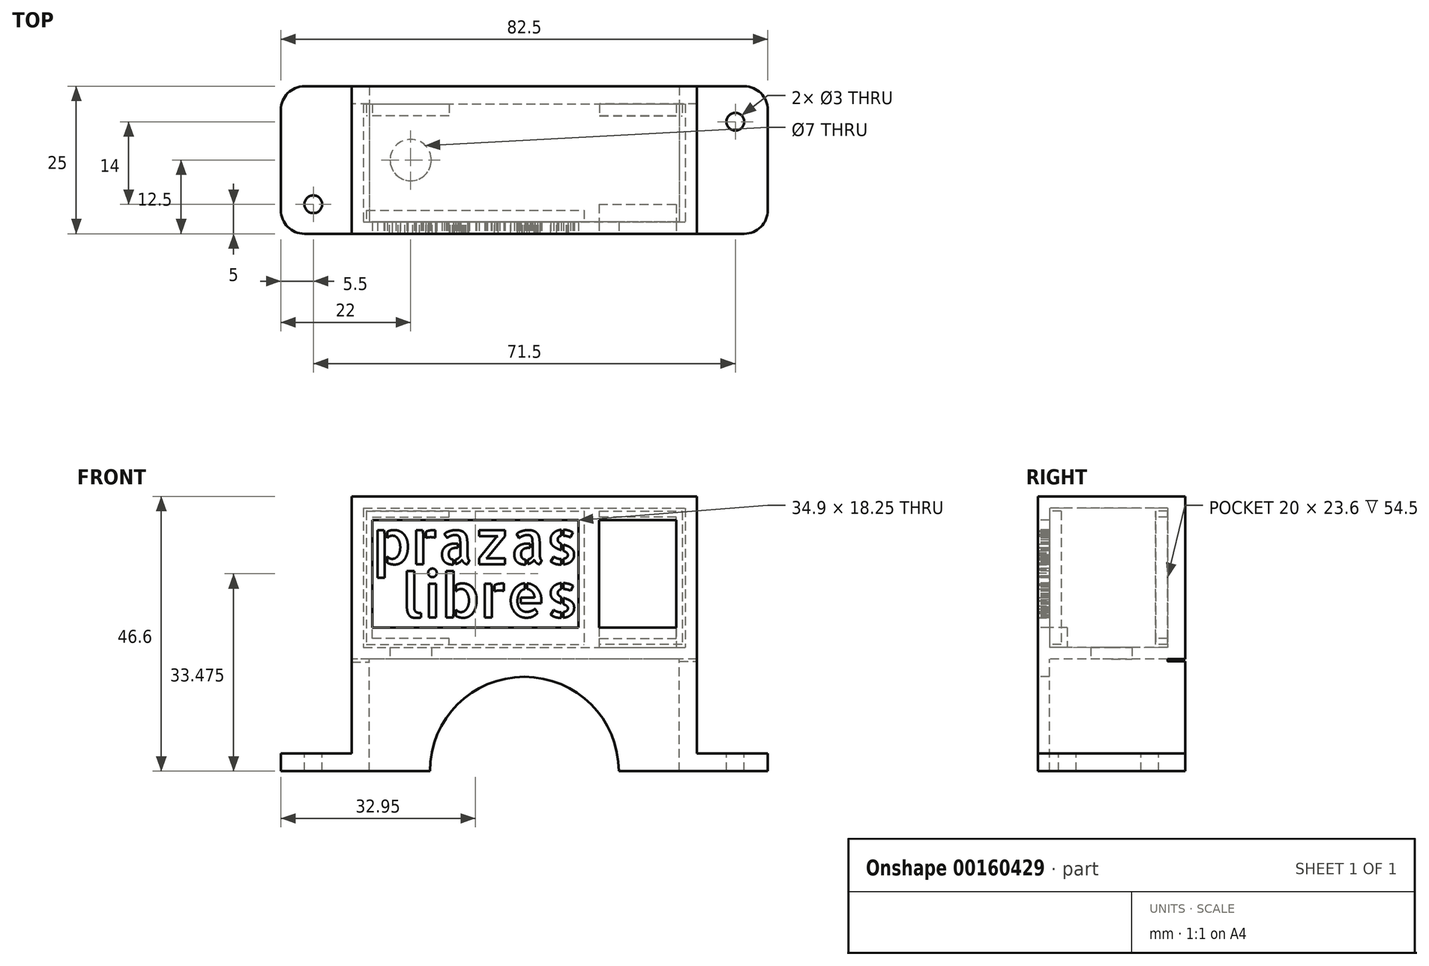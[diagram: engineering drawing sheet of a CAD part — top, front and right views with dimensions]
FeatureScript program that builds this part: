
annotation { "Feature Type Name" : "Feature", "Feature Type Description" : "" }
export const myFeature = defineFeature(function(context is Context, id is Id, definition is map)
    precondition{}
    {
        {
            var Q0;
            Q0=qCreatedBy(makeId("Front.planeOp"),FACE);
            var sketch = newSketch(context, id + "F0", { "sketchPlane" : qUnion([Q0])});
            skLineSegment(sketch, "E0.bottom", {"start": v(0, 0) * mm, "end": v(-58.5, 0) * mm});
            skLineSegment(sketch, "E0.top", {"start": v(0, 27.6) * mm, "end": v(-58.5, 27.6) * mm});
            skLineSegment(sketch, "E0.left", {"start": v(0, 0) * mm, "end": v(0, 27.6) * mm});
            skLineSegment(sketch, "E0.right", {"start": v(-58.5, 0) * mm, "end": v(-58.5, 27.6) * mm});
            skLineSegment(sketch, "E1.bottom", {"start": v(-3.5, 5.35) * mm, "end": v(-16.6, 5.35) * mm});
            skLineSegment(sketch, "E1.top", {"start": v(-3.5, 23.6) * mm, "end": v(-16.6, 23.6) * mm});
            skLineSegment(sketch, "E1.left", {"start": v(-3.5, 5.35) * mm, "end": v(-3.5, 23.6) * mm});
            skLineSegment(sketch, "E1.right", {"start": v(-16.6, 5.35) * mm, "end": v(-16.6, 23.6) * mm});
            skLineSegment(sketch, "E2", {"start": v(0, 0) * mm, "end": v(0, -16) * mm});
            skLineSegment(sketch, "E3", {"start": v(0, -16) * mm, "end": v(12, -16) * mm});
            skLineSegment(sketch, "E4", {"start": v(12, -16) * mm, "end": v(12, -19) * mm});
            skLineSegment(sketch, "E5", {"start": v(12, -19) * mm, "end": v(-3, -19) * mm});
            skLineSegment(sketch, "E6", {"start": v(-3, -19) * mm, "end": v(-3, 0) * mm});
            skLineSegment(sketch, "E7", {"start": v(-29.25, 49.54) * mm, "end": v(-29.25, -33.62) * mm, "construction": true});
            skLineSegment(sketch, "E8.MirrorCS", {"start": v(-58.5, 0) * mm, "end": v(-58.5, -16) * mm});
            skLineSegment(sketch, "E9.MirrorCS", {"start": v(-58.5, -16) * mm, "end": v(-70.5, -16) * mm});
            skLineSegment(sketch, "E10.MirrorCS", {"start": v(-70.5, -16) * mm, "end": v(-70.5, -19) * mm});
            skLineSegment(sketch, "E11.MirrorCS", {"start": v(-70.5, -19) * mm, "end": v(-55.5, -19) * mm});
            skLineSegment(sketch, "E12.MirrorCS", {"start": v(-55.5, -19) * mm, "end": v(-55.5, 0) * mm});
            skLineSegment(sketch, "E13.top", {"start": v(-56.5, 2) * mm, "end": v(-2, 2) * mm});
            skLineSegment(sketch, "E13.left", {"start": v(-56.5, 25.6) * mm, "end": v(-56.5, 2) * mm});
            skLineSegment(sketch, "E13.right", {"start": v(-2, 25.6) * mm, "end": v(-2, 2) * mm});
            skLineSegment(sketch, "E14", {"start": v(-55.5, -19) * mm, "end": v(-3, -19) * mm});
            skArc(sketch, "E15", {"start": v(-13.25, -19) * mm, "mid": v(-29.25, -3) * mm, "end": v(-45.25, -19) * mm});
            skLineSegment(sketch, "E16", {"start": v(-56.5, 25.6) * mm, "end": v(-2, 25.6) * mm});
            skLineSegment(sketch, "E17.bottom", {"start": v(-20.1, 23.6) * mm, "end": v(-55, 23.6) * mm});
            skLineSegment(sketch, "E17.top", {"start": v(-20.1, 5.35) * mm, "end": v(-55, 5.35) * mm});
            skLineSegment(sketch, "E17.left", {"start": v(-20.1, 23.6) * mm, "end": v(-20.1, 5.35) * mm});
            skLineSegment(sketch, "E17.right", {"start": v(-55, 23.6) * mm, "end": v(-55, 5.35) * mm});
            skLineSegment(sketch, "E18", {"start": v(-16.6, 5.35) * mm, "end": v(-16.6, 2) * mm});
            skLineSegment(sketch, "E19", {"start": v(-3.5, 5.35) * mm, "end": v(-3.5, 2) * mm});
            skLineSegment(sketch, "E20.bottom", {"start": v(-56, 25.1) * mm, "end": v(-19.1, 25.1) * mm});
            skLineSegment(sketch, "E20.top", {"start": v(-56, 2.5) * mm, "end": v(-19.1, 2.5) * mm});
            skLineSegment(sketch, "E20.left", {"start": v(-56, 25.1) * mm, "end": v(-56, 2.5) * mm});
            skLineSegment(sketch, "E20.right", {"start": v(-19.1, 25.1) * mm, "end": v(-19.1, 2.5) * mm});
            skText(sketch, "E21", { "text": "prazas", "fontName": "AllertaStencil-Regular.ttf"});
            skText(sketch, "E22", { "text": "libres", "fontName": "AllertaStencil-Regular.ttf"});
            skLineSegment(sketch, "E23", {"start": v(-3, -0.4) * mm, "end": v(0, -0.4) * mm});
            skLineSegment(sketch, "E24", {"start": v(-58.5, -0.5) * mm, "end": v(-55.5, -0.5) * mm});
            const initialGuessF0  = {"E21": [-0.055, 0.01608, 1, 0, 0.00752], "E22": [-0.05, 0.00705, 1, 0, 0.0075]};
            skSetInitialGuess(sketch, initialGuessF0);
            skSolve(sketch);
        }
        {
            var Q0;
            Q0=makeQuery(id+"F0.imprint","IMPRINT",FACE,{"disambiguationData":[TD([[makeQuery(id+"F0.imprint","IMPRINT",EDGE,{"derivedFrom":sQuery(id+"F0.wireOp",EDGE,"E0.top")}),1.0]])]});
            extrude(context, id + "F1", {"entities" : qUnion([Q0]), "oppositeDirection" : true, "depth" : 22 * mm});
        }
        {
            var Q0;
            Q0=makeQuery(id+"F0.imprint","IMPRINT",FACE,{"disambiguationData":[TD([[makeQuery(id+"F0.imprint","IMPRINT",EDGE,{"derivedFrom":sQuery(id+"F0.wireOp",EDGE,"1b1c06d7-5df4-4c5e-b730-0ffd46047cfb.sketch_text.stroke-0")}),-1.0]])]});
            var Q1;
            Q1=makeQuery(id+"F0.imprint","IMPRINT",FACE,{"disambiguationData":[TD([[makeQuery(id+"F0.imprint","IMPRINT",EDGE,{"derivedFrom":sQuery(id+"F0.wireOp",EDGE,"1b1c06d7-5df4-4c5e-b730-0ffd46047cfb.sketch_text.stroke-25")}),-1.0]])]});
            var Q2;
            Q2=makeQuery(id+"F0.imprint","IMPRINT",FACE,{"disambiguationData":[TD([[makeQuery(id+"F0.imprint","IMPRINT",EDGE,{"derivedFrom":sQuery(id+"F0.wireOp",EDGE,"1b1c06d7-5df4-4c5e-b730-0ffd46047cfb.sketch_text.stroke-16")}),1.0]])]});
            var Q3;
            Q3=makeQuery(id+"F0.imprint","IMPRINT",FACE,{"disambiguationData":[TD([[makeQuery(id+"F0.imprint","IMPRINT",EDGE,{"derivedFrom":sQuery(id+"F0.wireOp",EDGE,"1b1c06d7-5df4-4c5e-b730-0ffd46047cfb.sketch_text.stroke-38")}),-1.0]])]});
            var Q4;
            Q4=makeQuery(id+"F0.imprint","IMPRINT",FACE,{"disambiguationData":[TD([[makeQuery(id+"F0.imprint","IMPRINT",EDGE,{"derivedFrom":sQuery(id+"F0.wireOp",EDGE,"1b1c06d7-5df4-4c5e-b730-0ffd46047cfb.sketch_text.stroke-57")}),1.0]])]});
            var Q5;
            Q5=makeQuery(id+"F0.imprint","IMPRINT",FACE,{"disambiguationData":[TD([[makeQuery(id+"F0.imprint","IMPRINT",EDGE,{"derivedFrom":sQuery(id+"F0.wireOp",EDGE,"1b1c06d7-5df4-4c5e-b730-0ffd46047cfb.sketch_text.stroke-65")}),-1.0]])]});
            var Q6;
            Q6=makeQuery(id+"F0.imprint","IMPRINT",FACE,{"disambiguationData":[TD([[makeQuery(id+"F0.imprint","IMPRINT",EDGE,{"derivedFrom":sQuery(id+"F0.wireOp",EDGE,"1b1c06d7-5df4-4c5e-b730-0ffd46047cfb.sketch_text.stroke-75")}),-1.0]])]});
            var Q7;
            Q7=makeQuery(id+"F0.imprint","IMPRINT",FACE,{"disambiguationData":[TD([[makeQuery(id+"F0.imprint","IMPRINT",EDGE,{"derivedFrom":sQuery(id+"F0.wireOp",EDGE,"1b1c06d7-5df4-4c5e-b730-0ffd46047cfb.sketch_text.stroke-94")}),1.0]])]});
            var Q8;
            Q8=makeQuery(id+"F0.imprint","IMPRINT",FACE,{"disambiguationData":[TD([[makeQuery(id+"F0.imprint","IMPRINT",EDGE,{"derivedFrom":sQuery(id+"F0.wireOp",EDGE,"1b1c06d7-5df4-4c5e-b730-0ffd46047cfb.sketch_text.stroke-102")}),-1.0]])]});
            var Q9;
            Q9=makeQuery(id+"F0.imprint","IMPRINT",FACE,{"disambiguationData":[TD([[makeQuery(id+"F0.imprint","IMPRINT",EDGE,{"derivedFrom":sQuery(id+"F0.wireOp",EDGE,"71fc07e8-a1ba-411f-bdb7-0ce3e880cc4c.sketch_text.stroke-0")}),-1.0]])]});
            var Q10;
            Q10=makeQuery(id+"F0.imprint","IMPRINT",FACE,{"disambiguationData":[TD([[makeQuery(id+"F0.imprint","IMPRINT",EDGE,{"derivedFrom":sQuery(id+"F0.wireOp",EDGE,"71fc07e8-a1ba-411f-bdb7-0ce3e880cc4c.sketch_text.stroke-4")}),-1.0]])]});
            var Q11;
            Q11=makeQuery(id+"F0.imprint","IMPRINT",FACE,{"disambiguationData":[TD([[makeQuery(id+"F0.imprint","IMPRINT",EDGE,{"derivedFrom":sQuery(id+"F0.wireOp",EDGE,"71fc07e8-a1ba-411f-bdb7-0ce3e880cc4c.sketch_text.stroke-8")}),-1.0]])]});
            var Q12;
            Q12=makeQuery(id+"F0.imprint","IMPRINT",FACE,{"disambiguationData":[TD([[makeQuery(id+"F0.imprint","IMPRINT",EDGE,{"derivedFrom":sQuery(id+"F0.wireOp",EDGE,"71fc07e8-a1ba-411f-bdb7-0ce3e880cc4c.sketch_text.stroke-16")}),-1.0]])]});
            var Q13;
            Q13=makeQuery(id+"F0.imprint","IMPRINT",FACE,{"disambiguationData":[TD([[makeQuery(id+"F0.imprint","IMPRINT",EDGE,{"derivedFrom":sQuery(id+"F0.wireOp",EDGE,"71fc07e8-a1ba-411f-bdb7-0ce3e880cc4c.sketch_text.stroke-39")}),-1.0]])]});
            var Q14;
            Q14=makeQuery(id+"F0.imprint","IMPRINT",FACE,{"disambiguationData":[TD([[makeQuery(id+"F0.imprint","IMPRINT",EDGE,{"derivedFrom":sQuery(id+"F0.wireOp",EDGE,"71fc07e8-a1ba-411f-bdb7-0ce3e880cc4c.sketch_text.stroke-52")}),-1.0]])]});
            var Q15;
            Q15=makeQuery(id+"F0.imprint","IMPRINT",FACE,{"disambiguationData":[TD([[makeQuery(id+"F0.imprint","IMPRINT",EDGE,{"derivedFrom":sQuery(id+"F0.wireOp",EDGE,"71fc07e8-a1ba-411f-bdb7-0ce3e880cc4c.sketch_text.stroke-31")}),1.0]])]});
            var Q16;
            Q16=makeQuery(id+"F0.imprint","IMPRINT",FACE,{"disambiguationData":[TD([[makeQuery(id+"F0.imprint","IMPRINT",EDGE,{"derivedFrom":sQuery(id+"F0.wireOp",EDGE,"71fc07e8-a1ba-411f-bdb7-0ce3e880cc4c.sketch_text.stroke-66")}),1.0]])]});
            var Q17;
            Q17=makeQuery(id+"F0.imprint","IMPRINT",FACE,{"disambiguationData":[TD([[makeQuery(id+"F0.imprint","IMPRINT",EDGE,{"derivedFrom":sQuery(id+"F0.wireOp",EDGE,"71fc07e8-a1ba-411f-bdb7-0ce3e880cc4c.sketch_text.stroke-71")}),-1.0]])]});
            var Q18;
            Q18=makeQuery(id+"F0.imprint","IMPRINT",FACE,{"disambiguationData":[TD([[makeQuery(id+"F0.imprint","IMPRINT",EDGE,{"derivedFrom":sQuery(id+"F0.wireOp",EDGE,"c4529276-4a81-449c-a205-4a84c9b0bddf.sketch_text.stroke-0")}),-1.0]])]});
            var Q19;
            Q19=makeQuery(id+"F0.imprint","IMPRINT",FACE,{"disambiguationData":[TD([[makeQuery(id+"F0.imprint","IMPRINT",EDGE,{"derivedFrom":sQuery(id+"F0.wireOp",EDGE,"c4529276-4a81-449c-a205-4a84c9b0bddf.sketch_text.stroke-5")}),-1.0]])]});
            var Q20;
            Q20=makeQuery(id+"F0.imprint","IMPRINT",FACE,{"disambiguationData":[TD([[makeQuery(id+"F0.imprint","IMPRINT",EDGE,{"derivedFrom":sQuery(id+"F0.wireOp",EDGE,"c4529276-4a81-449c-a205-4a84c9b0bddf.sketch_text.stroke-31")}),-1.0]])]});
            var Q21;
            Q21=makeQuery(id+"F0.imprint","IMPRINT",FACE,{"disambiguationData":[TD([[makeQuery(id+"F0.imprint","IMPRINT",EDGE,{"derivedFrom":sQuery(id+"F0.wireOp",EDGE,"c4529276-4a81-449c-a205-4a84c9b0bddf.sketch_text.stroke-45")}),-1.0]])]});
            var Q22;
            Q22=makeQuery(id+"F0.imprint","IMPRINT",FACE,{"disambiguationData":[TD([[makeQuery(id+"F0.imprint","IMPRINT",EDGE,{"derivedFrom":sQuery(id+"F0.wireOp",EDGE,"c4529276-4a81-449c-a205-4a84c9b0bddf.sketch_text.stroke-38")}),-1.0]])]});
            var Q23;
            Q23=makeQuery(id+"F0.imprint","IMPRINT",FACE,{"disambiguationData":[TD([[makeQuery(id+"F0.imprint","IMPRINT",EDGE,{"derivedFrom":sQuery(id+"F0.wireOp",EDGE,"c4529276-4a81-449c-a205-4a84c9b0bddf.sketch_text.stroke-64")}),-1.0]])]});
            var Q24;
            Q24=makeQuery(id+"F0.imprint","IMPRINT",FACE,{"disambiguationData":[TD([[makeQuery(id+"F0.imprint","IMPRINT",EDGE,{"derivedFrom":sQuery(id+"F0.wireOp",EDGE,"c4529276-4a81-449c-a205-4a84c9b0bddf.sketch_text.stroke-100")}),-1.0]])]});
            var Q25;
            Q25=makeQuery(id+"F0.imprint","IMPRINT",FACE,{"disambiguationData":[TD([[makeQuery(id+"F0.imprint","IMPRINT",EDGE,{"derivedFrom":sQuery(id+"F0.wireOp",EDGE,"c4529276-4a81-449c-a205-4a84c9b0bddf.sketch_text.stroke-131")}),-1.0]])]});
            var Q26;
            Q26=makeQuery(id+"F0.imprint","IMPRINT",FACE,{"disambiguationData":[TD([[makeQuery(id+"F0.imprint","IMPRINT",EDGE,{"derivedFrom":sQuery(id+"F0.wireOp",EDGE,"c4529276-4a81-449c-a205-4a84c9b0bddf.sketch_text.stroke-112")}),-1.0]])]});
            var Q27;
            Q27=makeQuery(id+"F0.imprint","IMPRINT",FACE,{"disambiguationData":[TD([[makeQuery(id+"F0.imprint","IMPRINT",EDGE,{"derivedFrom":sQuery(id+"F0.wireOp",EDGE,"c4529276-4a81-449c-a205-4a84c9b0bddf.sketch_text.stroke-167")}),-1.0]])]});
            var Q28;
            Q28=makeQuery(id+"F0.imprint","IMPRINT",FACE,{"disambiguationData":[TD([[makeQuery(id+"F0.imprint","IMPRINT",EDGE,{"derivedFrom":sQuery(id+"F0.wireOp",EDGE,"c4529276-4a81-449c-a205-4a84c9b0bddf.sketch_text.stroke-181")}),-1.0]])]});
            var Q29;
            Q29=makeQuery(id+"F0.imprint","IMPRINT",FACE,{"disambiguationData":[TD([[makeQuery(id+"F0.imprint","IMPRINT",EDGE,{"derivedFrom":sQuery(id+"F0.wireOp",EDGE,"c4529276-4a81-449c-a205-4a84c9b0bddf.sketch_text.stroke-196")}),-1.0]])]});
            var Q30;
            Q30=makeQuery(id+"F0.imprint","IMPRINT",FACE,{"disambiguationData":[TD([[makeQuery(id+"F0.imprint","IMPRINT",EDGE,{"derivedFrom":sQuery(id+"F0.wireOp",EDGE,"c4529276-4a81-449c-a205-4a84c9b0bddf.sketch_text.stroke-187")}),-1.0]])]});
            var Q31;
            Q31=makeQuery(id+"F0.imprint","IMPRINT",FACE,{"disambiguationData":[TD([[makeQuery(id+"F0.imprint","IMPRINT",EDGE,{"derivedFrom":sQuery(id+"F0.wireOp",EDGE,"0c852f37-247c-4c24-b171-48b3ff05277b.sketch_text.stroke-0")}),-1.0]])]});
            var Q32;
            Q32=makeQuery(id+"F0.imprint","IMPRINT",FACE,{"disambiguationData":[TD([[makeQuery(id+"F0.imprint","IMPRINT",EDGE,{"derivedFrom":sQuery(id+"F0.wireOp",EDGE,"0c852f37-247c-4c24-b171-48b3ff05277b.sketch_text.stroke-22")}),-1.0]])]});
            var Q33;
            Q33=makeQuery(id+"F0.imprint","IMPRINT",FACE,{"disambiguationData":[TD([[makeQuery(id+"F0.imprint","IMPRINT",EDGE,{"derivedFrom":sQuery(id+"F0.wireOp",EDGE,"0c852f37-247c-4c24-b171-48b3ff05277b.sketch_text.stroke-18")}),-1.0]])]});
            var Q34;
            Q34=makeQuery(id+"F0.imprint","IMPRINT",FACE,{"disambiguationData":[TD([[makeQuery(id+"F0.imprint","IMPRINT",EDGE,{"derivedFrom":sQuery(id+"F0.wireOp",EDGE,"0c852f37-247c-4c24-b171-48b3ff05277b.sketch_text.stroke-30")}),-1.0]])]});
            var Q35;
            Q35=makeQuery(id+"F0.imprint","IMPRINT",FACE,{"disambiguationData":[TD([[makeQuery(id+"F0.imprint","IMPRINT",EDGE,{"derivedFrom":sQuery(id+"F0.wireOp",EDGE,"0c852f37-247c-4c24-b171-48b3ff05277b.sketch_text.stroke-36")}),-1.0]])]});
            var Q36;
            Q36=makeQuery(id+"F0.imprint","IMPRINT",FACE,{"disambiguationData":[TD([[makeQuery(id+"F0.imprint","IMPRINT",EDGE,{"derivedFrom":sQuery(id+"F0.wireOp",EDGE,"0c852f37-247c-4c24-b171-48b3ff05277b.sketch_text.stroke-63")}),-1.0]])]});
            var Q37;
            Q37=makeQuery(id+"F0.imprint","IMPRINT",FACE,{"disambiguationData":[TD([[makeQuery(id+"F0.imprint","IMPRINT",EDGE,{"derivedFrom":sQuery(id+"F0.wireOp",EDGE,"0c852f37-247c-4c24-b171-48b3ff05277b.sketch_text.stroke-70")}),-1.0]])]});
            var Q38;
            Q38=makeQuery(id+"F0.imprint","IMPRINT",FACE,{"disambiguationData":[TD([[makeQuery(id+"F0.imprint","IMPRINT",EDGE,{"derivedFrom":sQuery(id+"F0.wireOp",EDGE,"0c852f37-247c-4c24-b171-48b3ff05277b.sketch_text.stroke-90")}),-1.0]])]});
            var Q39;
            Q39=makeQuery(id+"F0.imprint","IMPRINT",FACE,{"disambiguationData":[TD([[makeQuery(id+"F0.imprint","IMPRINT",EDGE,{"derivedFrom":sQuery(id+"F0.wireOp",EDGE,"0c852f37-247c-4c24-b171-48b3ff05277b.sketch_text.stroke-77")}),-1.0]])]});
            var Q40;
            Q40=makeQuery(id+"F0.imprint","IMPRINT",FACE,{"disambiguationData":[TD([[makeQuery(id+"F0.imprint","IMPRINT",EDGE,{"derivedFrom":sQuery(id+"F0.wireOp",EDGE,"0c852f37-247c-4c24-b171-48b3ff05277b.sketch_text.stroke-114")}),-1.0]])]});
            var Q41;
            Q41=makeQuery(id+"F0.imprint","IMPRINT",FACE,{"disambiguationData":[TD([[makeQuery(id+"F0.imprint","IMPRINT",EDGE,{"derivedFrom":sQuery(id+"F0.wireOp",EDGE,"0c852f37-247c-4c24-b171-48b3ff05277b.sketch_text.stroke-128")}),-1.0]])]});
            var Q42;
            Q42=makeQuery(id+"F0.imprint","IMPRINT",FACE,{"disambiguationData":[TD([[makeQuery(id+"F0.imprint","IMPRINT",EDGE,{"derivedFrom":sQuery(id+"F0.wireOp",EDGE,"0c852f37-247c-4c24-b171-48b3ff05277b.sketch_text.stroke-143")}),-1.0]])]});
            var Q43;
            Q43=makeQuery(id+"F0.imprint","IMPRINT",FACE,{"disambiguationData":[TD([[makeQuery(id+"F0.imprint","IMPRINT",EDGE,{"derivedFrom":sQuery(id+"F0.wireOp",EDGE,"0c852f37-247c-4c24-b171-48b3ff05277b.sketch_text.stroke-134")}),-1.0]])]});
            var Q44;
            {var subQ1=sQuery(id+"F0.wireOp",EDGE,"E6");Q44=makeQuery(id+"F0.imprint","IMPRINT",FACE,{"disambiguationData":[TD([[makeQuery(id+"F0.imprint","IMPRINT",EDGE,{"derivedFrom":subQ1}),1.0]])]});}
            var Q45;
            {var subQ0=sQuery(id+"F0.wireOp",EDGE,"E2");Q45=makeQuery(id+"F0.imprint","IMPRINT",FACE,{"disambiguationData":[TD([[makeQuery(id+"F0.imprint","IMPRINT",EDGE,{"derivedFrom":subQ0}),-1.0]])]});}
            var Q46;
            {var subQ0=sQuery(id+"F0.wireOp",EDGE,"E8.MirrorCS");Q46=makeQuery(id+"F0.imprint","IMPRINT",FACE,{"disambiguationData":[TD([[makeQuery(id+"F0.imprint","IMPRINT",EDGE,{"derivedFrom":subQ0}),1.0]])]});}
            var Q47;
            {var subQ1=sQuery(id+"F0.wireOp",EDGE,"E12.MirrorCS");Q47=makeQuery(id+"F0.imprint","IMPRINT",FACE,{"disambiguationData":[TD([[makeQuery(id+"F0.imprint","IMPRINT",EDGE,{"derivedFrom":subQ1}),-1.0]])]});}
            var Q48;
            Q48=makeQuery(id+"F0.imprint","IMPRINT",FACE,{"disambiguationData":[TD([[makeQuery(id+"F0.imprint","IMPRINT",EDGE,{"derivedFrom":sQuery(id+"F0.wireOp",EDGE,"E1.top")}),-1.0]])]});
            var Q49;
            Q49=makeQuery(id+"F0.imprint","IMPRINT",FACE,{"disambiguationData":[TD([[makeQuery(id+"F0.imprint","IMPRINT",EDGE,{"derivedFrom":sQuery(id+"F0.wireOp",EDGE,"E1.bottom")}),1.0]])]});
            var Q50;
            Q50=makeQuery(id+"F0.imprint","IMPRINT",FACE,{"disambiguationData":[TD([[makeQuery(id+"F0.imprint","IMPRINT",EDGE,{"derivedFrom":sQuery(id+"F0.wireOp",EDGE,"E17.bottom")}),-1.0]])]});
            extrude(context, id + "F2", {"entities" : qUnion([Q0, Q1, Q2, Q3, Q4, Q5, Q6, Q7, Q8, Q9, Q10, Q11, Q12, Q13, Q14, Q15, Q16, Q17, Q18, Q19, Q20, Q21, Q22, Q23, Q24, Q25, Q26, Q27, Q28, Q29, Q30, Q31, Q32, Q33, Q34, Q35, Q36, Q37, Q38, Q39, Q40, Q41, Q42, Q43, Q44, Q45, Q46, Q47, Q48, Q49, Q50]), "operationType" : NewBodyOperationType.ADD, "oppositeDirection" : true, "depth" : 2 * mm});
        }
        {
            var Q0;
            {var subQ1=sQuery(id+"F0.wireOp",EDGE,"E9.MirrorCS");Q0=makeQuery(id+"F0.imprint","IMPRINT",FACE,{"disambiguationData":[TD([[makeQuery(id+"F0.imprint","IMPRINT",EDGE,{"derivedFrom":subQ1}),1.0]])]});}
            var Q1;
            {var subQ1=sQuery(id+"F0.wireOp",EDGE,"E3");Q1=makeQuery(id+"F0.imprint","IMPRINT",FACE,{"disambiguationData":[TD([[makeQuery(id+"F0.imprint","IMPRINT",EDGE,{"derivedFrom":subQ1}),-1.0]])]});}
            extrude(context, id + "F3", {"entities" : qUnion([Q0, Q1]), "operationType" : NewBodyOperationType.ADD, "oppositeDirection" : true, "depth" : 25 * mm});
        }
        {
            var Q0;
            Q0=makeQuery(id+"F0.imprint","IMPRINT",FACE,{"disambiguationData":[TD([[makeQuery(id+"F0.imprint","IMPRINT",EDGE,{"derivedFrom":sQuery(id+"F0.wireOp",EDGE,"1b1c06d7-5df4-4c5e-b730-0ffd46047cfb.sketch_text.stroke-0")}),-1.0]])]});
            var Q1;
            Q1=makeQuery(id+"F0.imprint","IMPRINT",FACE,{"disambiguationData":[TD([[makeQuery(id+"F0.imprint","IMPRINT",EDGE,{"derivedFrom":sQuery(id+"F0.wireOp",EDGE,"1b1c06d7-5df4-4c5e-b730-0ffd46047cfb.sketch_text.stroke-25")}),-1.0]])]});
            var Q2;
            Q2=makeQuery(id+"F0.imprint","IMPRINT",FACE,{"disambiguationData":[TD([[makeQuery(id+"F0.imprint","IMPRINT",EDGE,{"derivedFrom":sQuery(id+"F0.wireOp",EDGE,"1b1c06d7-5df4-4c5e-b730-0ffd46047cfb.sketch_text.stroke-38")}),-1.0]])]});
            var Q3;
            Q3=makeQuery(id+"F0.imprint","IMPRINT",FACE,{"disambiguationData":[TD([[makeQuery(id+"F0.imprint","IMPRINT",EDGE,{"derivedFrom":sQuery(id+"F0.wireOp",EDGE,"1b1c06d7-5df4-4c5e-b730-0ffd46047cfb.sketch_text.stroke-65")}),-1.0]])]});
            var Q4;
            Q4=makeQuery(id+"F0.imprint","IMPRINT",FACE,{"disambiguationData":[TD([[makeQuery(id+"F0.imprint","IMPRINT",EDGE,{"derivedFrom":sQuery(id+"F0.wireOp",EDGE,"1b1c06d7-5df4-4c5e-b730-0ffd46047cfb.sketch_text.stroke-75")}),-1.0]])]});
            var Q5;
            Q5=makeQuery(id+"F0.imprint","IMPRINT",FACE,{"disambiguationData":[TD([[makeQuery(id+"F0.imprint","IMPRINT",EDGE,{"derivedFrom":sQuery(id+"F0.wireOp",EDGE,"1b1c06d7-5df4-4c5e-b730-0ffd46047cfb.sketch_text.stroke-102")}),-1.0]])]});
            var Q6;
            Q6=makeQuery(id+"F0.imprint","IMPRINT",FACE,{"disambiguationData":[TD([[makeQuery(id+"F0.imprint","IMPRINT",EDGE,{"derivedFrom":sQuery(id+"F0.wireOp",EDGE,"71fc07e8-a1ba-411f-bdb7-0ce3e880cc4c.sketch_text.stroke-0")}),-1.0]])]});
            var Q7;
            Q7=makeQuery(id+"F0.imprint","IMPRINT",FACE,{"disambiguationData":[TD([[makeQuery(id+"F0.imprint","IMPRINT",EDGE,{"derivedFrom":sQuery(id+"F0.wireOp",EDGE,"71fc07e8-a1ba-411f-bdb7-0ce3e880cc4c.sketch_text.stroke-4")}),-1.0]])]});
            var Q8;
            Q8=makeQuery(id+"F0.imprint","IMPRINT",FACE,{"disambiguationData":[TD([[makeQuery(id+"F0.imprint","IMPRINT",EDGE,{"derivedFrom":sQuery(id+"F0.wireOp",EDGE,"71fc07e8-a1ba-411f-bdb7-0ce3e880cc4c.sketch_text.stroke-8")}),-1.0]])]});
            var Q9;
            Q9=makeQuery(id+"F0.imprint","IMPRINT",FACE,{"disambiguationData":[TD([[makeQuery(id+"F0.imprint","IMPRINT",EDGE,{"derivedFrom":sQuery(id+"F0.wireOp",EDGE,"71fc07e8-a1ba-411f-bdb7-0ce3e880cc4c.sketch_text.stroke-16")}),-1.0]])]});
            var Q10;
            Q10=makeQuery(id+"F0.imprint","IMPRINT",FACE,{"disambiguationData":[TD([[makeQuery(id+"F0.imprint","IMPRINT",EDGE,{"derivedFrom":sQuery(id+"F0.wireOp",EDGE,"71fc07e8-a1ba-411f-bdb7-0ce3e880cc4c.sketch_text.stroke-39")}),-1.0]])]});
            var Q11;
            Q11=makeQuery(id+"F0.imprint","IMPRINT",FACE,{"disambiguationData":[TD([[makeQuery(id+"F0.imprint","IMPRINT",EDGE,{"derivedFrom":sQuery(id+"F0.wireOp",EDGE,"71fc07e8-a1ba-411f-bdb7-0ce3e880cc4c.sketch_text.stroke-52")}),-1.0]])]});
            var Q12;
            Q12=makeQuery(id+"F0.imprint","IMPRINT",FACE,{"disambiguationData":[TD([[makeQuery(id+"F0.imprint","IMPRINT",EDGE,{"derivedFrom":sQuery(id+"F0.wireOp",EDGE,"71fc07e8-a1ba-411f-bdb7-0ce3e880cc4c.sketch_text.stroke-71")}),-1.0]])]});
            var Q13;
            Q13=makeQuery(id+"F0.imprint","IMPRINT",FACE,{"disambiguationData":[TD([[makeQuery(id+"F0.imprint","IMPRINT",EDGE,{"derivedFrom":sQuery(id+"F0.wireOp",EDGE,"71fc07e8-a1ba-411f-bdb7-0ce3e880cc4c.sketch_text.stroke-66")}),1.0]])]});
            var Q14;
            Q14=makeQuery(id+"F0.imprint","IMPRINT",FACE,{"disambiguationData":[TD([[makeQuery(id+"F0.imprint","IMPRINT",EDGE,{"derivedFrom":sQuery(id+"F0.wireOp",EDGE,"71fc07e8-a1ba-411f-bdb7-0ce3e880cc4c.sketch_text.stroke-31")}),1.0]])]});
            var Q15;
            Q15=makeQuery(id+"F0.imprint","IMPRINT",FACE,{"disambiguationData":[TD([[makeQuery(id+"F0.imprint","IMPRINT",EDGE,{"derivedFrom":sQuery(id+"F0.wireOp",EDGE,"1b1c06d7-5df4-4c5e-b730-0ffd46047cfb.sketch_text.stroke-57")}),1.0]])]});
            var Q16;
            Q16=makeQuery(id+"F0.imprint","IMPRINT",FACE,{"disambiguationData":[TD([[makeQuery(id+"F0.imprint","IMPRINT",EDGE,{"derivedFrom":sQuery(id+"F0.wireOp",EDGE,"1b1c06d7-5df4-4c5e-b730-0ffd46047cfb.sketch_text.stroke-16")}),1.0]])]});
            var Q17;
            Q17=makeQuery(id+"F0.imprint","IMPRINT",FACE,{"disambiguationData":[TD([[makeQuery(id+"F0.imprint","IMPRINT",EDGE,{"derivedFrom":sQuery(id+"F0.wireOp",EDGE,"1b1c06d7-5df4-4c5e-b730-0ffd46047cfb.sketch_text.stroke-94")}),1.0]])]});
            var Q18;
            Q18=makeQuery(id+"F0.imprint","IMPRINT",FACE,{"disambiguationData":[TD([[makeQuery(id+"F0.imprint","IMPRINT",EDGE,{"derivedFrom":sQuery(id+"F0.wireOp",EDGE,"E0.top")}),1.0]])]});
            var Q19;
            Q19=makeQuery(id+"F0.imprint","IMPRINT",FACE,{"disambiguationData":[TD([[makeQuery(id+"F0.imprint","IMPRINT",EDGE,{"derivedFrom":sQuery(id+"F0.wireOp",EDGE,"c4529276-4a81-449c-a205-4a84c9b0bddf.sketch_text.stroke-5")}),-1.0]])]});
            var Q20;
            Q20=makeQuery(id+"F0.imprint","IMPRINT",FACE,{"disambiguationData":[TD([[makeQuery(id+"F0.imprint","IMPRINT",EDGE,{"derivedFrom":sQuery(id+"F0.wireOp",EDGE,"c4529276-4a81-449c-a205-4a84c9b0bddf.sketch_text.stroke-0")}),-1.0]])]});
            var Q21;
            Q21=makeQuery(id+"F0.imprint","IMPRINT",FACE,{"disambiguationData":[TD([[makeQuery(id+"F0.imprint","IMPRINT",EDGE,{"derivedFrom":sQuery(id+"F0.wireOp",EDGE,"c4529276-4a81-449c-a205-4a84c9b0bddf.sketch_text.stroke-31")}),-1.0]])]});
            var Q22;
            Q22=makeQuery(id+"F0.imprint","IMPRINT",FACE,{"disambiguationData":[TD([[makeQuery(id+"F0.imprint","IMPRINT",EDGE,{"derivedFrom":sQuery(id+"F0.wireOp",EDGE,"c4529276-4a81-449c-a205-4a84c9b0bddf.sketch_text.stroke-38")}),-1.0]])]});
            var Q23;
            Q23=makeQuery(id+"F0.imprint","IMPRINT",FACE,{"disambiguationData":[TD([[makeQuery(id+"F0.imprint","IMPRINT",EDGE,{"derivedFrom":sQuery(id+"F0.wireOp",EDGE,"c4529276-4a81-449c-a205-4a84c9b0bddf.sketch_text.stroke-64")}),-1.0]])]});
            var Q24;
            Q24=makeQuery(id+"F0.imprint","IMPRINT",FACE,{"disambiguationData":[TD([[makeQuery(id+"F0.imprint","IMPRINT",EDGE,{"derivedFrom":sQuery(id+"F0.wireOp",EDGE,"c4529276-4a81-449c-a205-4a84c9b0bddf.sketch_text.stroke-45")}),-1.0]])]});
            var Q25;
            Q25=makeQuery(id+"F0.imprint","IMPRINT",FACE,{"disambiguationData":[TD([[makeQuery(id+"F0.imprint","IMPRINT",EDGE,{"derivedFrom":sQuery(id+"F0.wireOp",EDGE,"c4529276-4a81-449c-a205-4a84c9b0bddf.sketch_text.stroke-100")}),-1.0]])]});
            var Q26;
            Q26=makeQuery(id+"F0.imprint","IMPRINT",FACE,{"disambiguationData":[TD([[makeQuery(id+"F0.imprint","IMPRINT",EDGE,{"derivedFrom":sQuery(id+"F0.wireOp",EDGE,"c4529276-4a81-449c-a205-4a84c9b0bddf.sketch_text.stroke-131")}),-1.0]])]});
            var Q27;
            Q27=makeQuery(id+"F0.imprint","IMPRINT",FACE,{"disambiguationData":[TD([[makeQuery(id+"F0.imprint","IMPRINT",EDGE,{"derivedFrom":sQuery(id+"F0.wireOp",EDGE,"c4529276-4a81-449c-a205-4a84c9b0bddf.sketch_text.stroke-112")}),-1.0]])]});
            var Q28;
            Q28=makeQuery(id+"F0.imprint","IMPRINT",FACE,{"disambiguationData":[TD([[makeQuery(id+"F0.imprint","IMPRINT",EDGE,{"derivedFrom":sQuery(id+"F0.wireOp",EDGE,"c4529276-4a81-449c-a205-4a84c9b0bddf.sketch_text.stroke-167")}),-1.0]])]});
            var Q29;
            Q29=makeQuery(id+"F0.imprint","IMPRINT",FACE,{"disambiguationData":[TD([[makeQuery(id+"F0.imprint","IMPRINT",EDGE,{"derivedFrom":sQuery(id+"F0.wireOp",EDGE,"c4529276-4a81-449c-a205-4a84c9b0bddf.sketch_text.stroke-181")}),-1.0]])]});
            var Q30;
            Q30=makeQuery(id+"F0.imprint","IMPRINT",FACE,{"disambiguationData":[TD([[makeQuery(id+"F0.imprint","IMPRINT",EDGE,{"derivedFrom":sQuery(id+"F0.wireOp",EDGE,"c4529276-4a81-449c-a205-4a84c9b0bddf.sketch_text.stroke-196")}),-1.0]])]});
            var Q31;
            Q31=makeQuery(id+"F0.imprint","IMPRINT",FACE,{"disambiguationData":[TD([[makeQuery(id+"F0.imprint","IMPRINT",EDGE,{"derivedFrom":sQuery(id+"F0.wireOp",EDGE,"c4529276-4a81-449c-a205-4a84c9b0bddf.sketch_text.stroke-187")}),-1.0]])]});
            var Q32;
            Q32=makeQuery(id+"F0.imprint","IMPRINT",FACE,{"disambiguationData":[TD([[makeQuery(id+"F0.imprint","IMPRINT",EDGE,{"derivedFrom":sQuery(id+"F0.wireOp",EDGE,"0c852f37-247c-4c24-b171-48b3ff05277b.sketch_text.stroke-0")}),-1.0]])]});
            var Q33;
            Q33=makeQuery(id+"F0.imprint","IMPRINT",FACE,{"disambiguationData":[TD([[makeQuery(id+"F0.imprint","IMPRINT",EDGE,{"derivedFrom":sQuery(id+"F0.wireOp",EDGE,"0c852f37-247c-4c24-b171-48b3ff05277b.sketch_text.stroke-18")}),-1.0]])]});
            var Q34;
            Q34=makeQuery(id+"F0.imprint","IMPRINT",FACE,{"disambiguationData":[TD([[makeQuery(id+"F0.imprint","IMPRINT",EDGE,{"derivedFrom":sQuery(id+"F0.wireOp",EDGE,"0c852f37-247c-4c24-b171-48b3ff05277b.sketch_text.stroke-22")}),-1.0]])]});
            var Q35;
            Q35=makeQuery(id+"F0.imprint","IMPRINT",FACE,{"disambiguationData":[TD([[makeQuery(id+"F0.imprint","IMPRINT",EDGE,{"derivedFrom":sQuery(id+"F0.wireOp",EDGE,"0c852f37-247c-4c24-b171-48b3ff05277b.sketch_text.stroke-30")}),-1.0]])]});
            var Q36;
            Q36=makeQuery(id+"F0.imprint","IMPRINT",FACE,{"disambiguationData":[TD([[makeQuery(id+"F0.imprint","IMPRINT",EDGE,{"derivedFrom":sQuery(id+"F0.wireOp",EDGE,"0c852f37-247c-4c24-b171-48b3ff05277b.sketch_text.stroke-36")}),-1.0]])]});
            var Q37;
            Q37=makeQuery(id+"F0.imprint","IMPRINT",FACE,{"disambiguationData":[TD([[makeQuery(id+"F0.imprint","IMPRINT",EDGE,{"derivedFrom":sQuery(id+"F0.wireOp",EDGE,"0c852f37-247c-4c24-b171-48b3ff05277b.sketch_text.stroke-63")}),-1.0]])]});
            var Q38;
            Q38=makeQuery(id+"F0.imprint","IMPRINT",FACE,{"disambiguationData":[TD([[makeQuery(id+"F0.imprint","IMPRINT",EDGE,{"derivedFrom":sQuery(id+"F0.wireOp",EDGE,"0c852f37-247c-4c24-b171-48b3ff05277b.sketch_text.stroke-70")}),-1.0]])]});
            var Q39;
            Q39=makeQuery(id+"F0.imprint","IMPRINT",FACE,{"disambiguationData":[TD([[makeQuery(id+"F0.imprint","IMPRINT",EDGE,{"derivedFrom":sQuery(id+"F0.wireOp",EDGE,"0c852f37-247c-4c24-b171-48b3ff05277b.sketch_text.stroke-90")}),-1.0]])]});
            var Q40;
            Q40=makeQuery(id+"F0.imprint","IMPRINT",FACE,{"disambiguationData":[TD([[makeQuery(id+"F0.imprint","IMPRINT",EDGE,{"derivedFrom":sQuery(id+"F0.wireOp",EDGE,"0c852f37-247c-4c24-b171-48b3ff05277b.sketch_text.stroke-77")}),-1.0]])]});
            var Q41;
            Q41=makeQuery(id+"F0.imprint","IMPRINT",FACE,{"disambiguationData":[TD([[makeQuery(id+"F0.imprint","IMPRINT",EDGE,{"derivedFrom":sQuery(id+"F0.wireOp",EDGE,"0c852f37-247c-4c24-b171-48b3ff05277b.sketch_text.stroke-114")}),-1.0]])]});
            var Q42;
            Q42=makeQuery(id+"F0.imprint","IMPRINT",FACE,{"disambiguationData":[TD([[makeQuery(id+"F0.imprint","IMPRINT",EDGE,{"derivedFrom":sQuery(id+"F0.wireOp",EDGE,"0c852f37-247c-4c24-b171-48b3ff05277b.sketch_text.stroke-128")}),-1.0]])]});
            var Q43;
            Q43=makeQuery(id+"F0.imprint","IMPRINT",FACE,{"disambiguationData":[TD([[makeQuery(id+"F0.imprint","IMPRINT",EDGE,{"derivedFrom":sQuery(id+"F0.wireOp",EDGE,"0c852f37-247c-4c24-b171-48b3ff05277b.sketch_text.stroke-143")}),-1.0]])]});
            var Q44;
            Q44=makeQuery(id+"F0.imprint","IMPRINT",FACE,{"disambiguationData":[TD([[makeQuery(id+"F0.imprint","IMPRINT",EDGE,{"derivedFrom":sQuery(id+"F0.wireOp",EDGE,"0c852f37-247c-4c24-b171-48b3ff05277b.sketch_text.stroke-134")}),-1.0]])]});
            var Q45;
            Q45=makeQuery(id+"F0.imprint","IMPRINT",FACE,{"disambiguationData":[TD([[makeQuery(id+"F0.imprint","IMPRINT",EDGE,{"derivedFrom":sQuery(id+"F0.wireOp",EDGE,"E1.bottom")}),-1.0]])]});
            var Q46;
            Q46=makeQuery(id+"F0.imprint","IMPRINT",FACE,{"disambiguationData":[TD([[makeQuery(id+"F0.imprint","IMPRINT",EDGE,{"derivedFrom":sQuery(id+"F0.wireOp",EDGE,"E1.top")}),-1.0]])]});
            var Q47;
            Q47=makeQuery(id+"F0.imprint","IMPRINT",FACE,{"disambiguationData":[TD([[makeQuery(id+"F0.imprint","IMPRINT",EDGE,{"derivedFrom":sQuery(id+"F0.wireOp",EDGE,"E1.bottom")}),1.0]])]});
            var Q48;
            Q48=makeQuery(id+"F0.imprint","IMPRINT",FACE,{"disambiguationData":[TD([[makeQuery(id+"F0.imprint","IMPRINT",EDGE,{"derivedFrom":sQuery(id+"F0.wireOp",EDGE,"E17.bottom")}),1.0]])]});
            var Q49;
            Q49=makeQuery(id+"F0.imprint","IMPRINT",FACE,{"disambiguationData":[TD([[makeQuery(id+"F0.imprint","IMPRINT",EDGE,{"derivedFrom":sQuery(id+"F0.wireOp",EDGE,"E17.bottom")}),-1.0]])]});
            var Q50;
            Q50=makeQuery(id+"F0.imprint","IMPRINT",FACE,{"disambiguationData":[TD([[makeQuery(id+"F0.imprint","IMPRINT",EDGE,{"derivedFrom":sQuery(id+"F0.wireOp",EDGE,"E21.sketch_text.stroke-0")}),-1.0]])]});
            var Q51;
            Q51=makeQuery(id+"F0.imprint","IMPRINT",FACE,{"disambiguationData":[TD([[makeQuery(id+"F0.imprint","IMPRINT",EDGE,{"derivedFrom":sQuery(id+"F0.wireOp",EDGE,"E21.sketch_text.stroke-5")}),-1.0]])]});
            var Q52;
            Q52=makeQuery(id+"F0.imprint","IMPRINT",FACE,{"disambiguationData":[TD([[makeQuery(id+"F0.imprint","IMPRINT",EDGE,{"derivedFrom":sQuery(id+"F0.wireOp",EDGE,"E21.sketch_text.stroke-31")}),-1.0]])]});
            var Q53;
            Q53=makeQuery(id+"F0.imprint","IMPRINT",FACE,{"disambiguationData":[TD([[makeQuery(id+"F0.imprint","IMPRINT",EDGE,{"derivedFrom":sQuery(id+"F0.wireOp",EDGE,"E21.sketch_text.stroke-38")}),-1.0]])]});
            var Q54;
            Q54=makeQuery(id+"F0.imprint","IMPRINT",FACE,{"disambiguationData":[TD([[makeQuery(id+"F0.imprint","IMPRINT",EDGE,{"derivedFrom":sQuery(id+"F0.wireOp",EDGE,"E21.sketch_text.stroke-64")}),-1.0]])]});
            var Q55;
            Q55=makeQuery(id+"F0.imprint","IMPRINT",FACE,{"disambiguationData":[TD([[makeQuery(id+"F0.imprint","IMPRINT",EDGE,{"derivedFrom":sQuery(id+"F0.wireOp",EDGE,"E21.sketch_text.stroke-45")}),-1.0]])]});
            var Q56;
            Q56=makeQuery(id+"F0.imprint","IMPRINT",FACE,{"disambiguationData":[TD([[makeQuery(id+"F0.imprint","IMPRINT",EDGE,{"derivedFrom":sQuery(id+"F0.wireOp",EDGE,"E21.sketch_text.stroke-100")}),-1.0]])]});
            var Q57;
            Q57=makeQuery(id+"F0.imprint","IMPRINT",FACE,{"disambiguationData":[TD([[makeQuery(id+"F0.imprint","IMPRINT",EDGE,{"derivedFrom":sQuery(id+"F0.wireOp",EDGE,"E21.sketch_text.stroke-131")}),-1.0]])]});
            var Q58;
            Q58=makeQuery(id+"F0.imprint","IMPRINT",FACE,{"disambiguationData":[TD([[makeQuery(id+"F0.imprint","IMPRINT",EDGE,{"derivedFrom":sQuery(id+"F0.wireOp",EDGE,"E21.sketch_text.stroke-112")}),-1.0]])]});
            var Q59;
            Q59=makeQuery(id+"F0.imprint","IMPRINT",FACE,{"disambiguationData":[TD([[makeQuery(id+"F0.imprint","IMPRINT",EDGE,{"derivedFrom":sQuery(id+"F0.wireOp",EDGE,"E21.sketch_text.stroke-167")}),-1.0]])]});
            var Q60;
            Q60=makeQuery(id+"F0.imprint","IMPRINT",FACE,{"disambiguationData":[TD([[makeQuery(id+"F0.imprint","IMPRINT",EDGE,{"derivedFrom":sQuery(id+"F0.wireOp",EDGE,"E21.sketch_text.stroke-181")}),-1.0]])]});
            var Q61;
            Q61=makeQuery(id+"F0.imprint","IMPRINT",FACE,{"disambiguationData":[TD([[makeQuery(id+"F0.imprint","IMPRINT",EDGE,{"derivedFrom":sQuery(id+"F0.wireOp",EDGE,"E21.sketch_text.stroke-196")}),-1.0]])]});
            var Q62;
            Q62=makeQuery(id+"F0.imprint","IMPRINT",FACE,{"disambiguationData":[TD([[makeQuery(id+"F0.imprint","IMPRINT",EDGE,{"derivedFrom":sQuery(id+"F0.wireOp",EDGE,"E21.sketch_text.stroke-187")}),-1.0]])]});
            var Q63;
            Q63=makeQuery(id+"F0.imprint","IMPRINT",FACE,{"disambiguationData":[TD([[makeQuery(id+"F0.imprint","IMPRINT",EDGE,{"derivedFrom":sQuery(id+"F0.wireOp",EDGE,"E22.sketch_text.stroke-0")}),-1.0]])]});
            var Q64;
            Q64=makeQuery(id+"F0.imprint","IMPRINT",FACE,{"disambiguationData":[TD([[makeQuery(id+"F0.imprint","IMPRINT",EDGE,{"derivedFrom":sQuery(id+"F0.wireOp",EDGE,"E22.sketch_text.stroke-18")}),-1.0]])]});
            var Q65;
            Q65=makeQuery(id+"F0.imprint","IMPRINT",FACE,{"disambiguationData":[TD([[makeQuery(id+"F0.imprint","IMPRINT",EDGE,{"derivedFrom":sQuery(id+"F0.wireOp",EDGE,"E22.sketch_text.stroke-30")}),-1.0]])]});
            var Q66;
            Q66=makeQuery(id+"F0.imprint","IMPRINT",FACE,{"disambiguationData":[TD([[makeQuery(id+"F0.imprint","IMPRINT",EDGE,{"derivedFrom":sQuery(id+"F0.wireOp",EDGE,"E22.sketch_text.stroke-22")}),-1.0]])]});
            var Q67;
            Q67=makeQuery(id+"F0.imprint","IMPRINT",FACE,{"disambiguationData":[TD([[makeQuery(id+"F0.imprint","IMPRINT",EDGE,{"derivedFrom":sQuery(id+"F0.wireOp",EDGE,"E22.sketch_text.stroke-36")}),-1.0]])]});
            var Q68;
            Q68=makeQuery(id+"F0.imprint","IMPRINT",FACE,{"disambiguationData":[TD([[makeQuery(id+"F0.imprint","IMPRINT",EDGE,{"derivedFrom":sQuery(id+"F0.wireOp",EDGE,"E22.sketch_text.stroke-63")}),-1.0]])]});
            var Q69;
            Q69=makeQuery(id+"F0.imprint","IMPRINT",FACE,{"disambiguationData":[TD([[makeQuery(id+"F0.imprint","IMPRINT",EDGE,{"derivedFrom":sQuery(id+"F0.wireOp",EDGE,"E22.sketch_text.stroke-70")}),-1.0]])]});
            var Q70;
            Q70=makeQuery(id+"F0.imprint","IMPRINT",FACE,{"disambiguationData":[TD([[makeQuery(id+"F0.imprint","IMPRINT",EDGE,{"derivedFrom":sQuery(id+"F0.wireOp",EDGE,"E22.sketch_text.stroke-90")}),-1.0]])]});
            var Q71;
            Q71=makeQuery(id+"F0.imprint","IMPRINT",FACE,{"disambiguationData":[TD([[makeQuery(id+"F0.imprint","IMPRINT",EDGE,{"derivedFrom":sQuery(id+"F0.wireOp",EDGE,"E22.sketch_text.stroke-77")}),-1.0]])]});
            var Q72;
            Q72=makeQuery(id+"F0.imprint","IMPRINT",FACE,{"disambiguationData":[TD([[makeQuery(id+"F0.imprint","IMPRINT",EDGE,{"derivedFrom":sQuery(id+"F0.wireOp",EDGE,"E22.sketch_text.stroke-114")}),-1.0]])]});
            var Q73;
            Q73=makeQuery(id+"F0.imprint","IMPRINT",FACE,{"disambiguationData":[TD([[makeQuery(id+"F0.imprint","IMPRINT",EDGE,{"derivedFrom":sQuery(id+"F0.wireOp",EDGE,"E22.sketch_text.stroke-128")}),-1.0]])]});
            var Q74;
            Q74=makeQuery(id+"F0.imprint","IMPRINT",FACE,{"disambiguationData":[TD([[makeQuery(id+"F0.imprint","IMPRINT",EDGE,{"derivedFrom":sQuery(id+"F0.wireOp",EDGE,"E22.sketch_text.stroke-143")}),-1.0]])]});
            var Q75;
            Q75=makeQuery(id+"F0.imprint","IMPRINT",FACE,{"disambiguationData":[TD([[makeQuery(id+"F0.imprint","IMPRINT",EDGE,{"derivedFrom":sQuery(id+"F0.wireOp",EDGE,"E22.sketch_text.stroke-134")}),-1.0]])]});
            extrude(context, id + "F4", {"entities" : qUnion([Q0, Q1, Q2, Q3, Q4, Q5, Q6, Q7, Q8, Q9, Q10, Q11, Q12, Q13, Q14, Q15, Q16, Q17, Q18, Q19, Q20, Q21, Q22, Q23, Q24, Q25, Q26, Q27, Q28, Q29, Q30, Q31, Q32, Q33, Q34, Q35, Q36, Q37, Q38, Q39, Q40, Q41, Q42, Q43, Q44, Q45, Q46, Q47, Q48, Q49, Q50, Q51, Q52, Q53, Q54, Q55, Q56, Q57, Q58, Q59, Q60, Q61, Q62, Q63, Q64, Q65, Q66, Q67, Q68, Q69, Q70, Q71, Q72, Q73, Q74, Q75]), "oppositeDirection" : true, "depth" : 25 * mm, "hasSecondDirection" : true, "secondDirectionOppositeDirection" : true, "secondDirectionDepth" : 22 * mm});
        }
        {
            var Q0;
            Q0=qCreatedBy(makeId("Front.planeOp"),FACE);
            var sketch = newSketch(context, id + "F5", { "sketchPlane" : qUnion([Q0])});
            skLineSegment(sketch, "E25", {"start": v(-56, 25.1) * mm, "end": v(-56, 2.5) * mm});
            skLineSegment(sketch, "E26", {"start": v(-56, 2.5) * mm, "end": v(-42, 2.5) * mm});
            skLineSegment(sketch, "E27", {"start": v(-42, 2.5) * mm, "end": v(-42, 3.5) * mm});
            skLineSegment(sketch, "E28", {"start": v(-42, 3.5) * mm, "end": v(-55, 3.5) * mm});
            skLineSegment(sketch, "E29", {"start": v(-55, 3.5) * mm, "end": v(-55, 24.1) * mm});
            skLineSegment(sketch, "E30", {"start": v(-55, 24.1) * mm, "end": v(-42, 24.1) * mm});
            skLineSegment(sketch, "E31", {"start": v(-42, 24.1) * mm, "end": v(-42, 25.1) * mm});
            skLineSegment(sketch, "E32", {"start": v(-42, 25.1) * mm, "end": v(-56, 25.1) * mm});
            skLineSegment(sketch, "E33.MirrorCS", {"start": v(-16.5, 2.5) * mm, "end": v(-16.5, 3.5) * mm});
            skLineSegment(sketch, "E34.MirrorCS", {"start": v(-16.5, 24.1) * mm, "end": v(-16.5, 25.1) * mm});
            skLineSegment(sketch, "E35.MirrorCS", {"start": v(-2.5, 25.1) * mm, "end": v(-2.5, 2.5) * mm});
            skLineSegment(sketch, "E36.MirrorCS", {"start": v(-16.5, 25.1) * mm, "end": v(-2.5, 25.1) * mm});
            skLineSegment(sketch, "E37.MirrorCS", {"start": v(-3.5, 3.5) * mm, "end": v(-3.5, 24.1) * mm});
            skLineSegment(sketch, "E38.MirrorCS", {"start": v(-3.5, 24.1) * mm, "end": v(-16.5, 24.1) * mm});
            skLineSegment(sketch, "E39.MirrorCS", {"start": v(-2.5, 2.5) * mm, "end": v(-16.5, 2.5) * mm});
            skLineSegment(sketch, "E40.MirrorCS", {"start": v(-16.5, 3.5) * mm, "end": v(-3.5, 3.5) * mm});
            skSolve(sketch);
        }
        {
            var Q0;
            Q0=makeQuery(id+"F5.imprint","IMPRINT",FACE,{"disambiguationData":[TD([[makeQuery(id+"F5.imprint","IMPRINT",EDGE,{"derivedFrom":sQuery(id+"F5.wireOp",EDGE,"E25")}),1.0]])]});
            var Q1;
            Q1=makeQuery(id+"F5.imprint","IMPRINT",FACE,{"disambiguationData":[TD([[makeQuery(id+"F5.imprint","IMPRINT",EDGE,{"derivedFrom":sQuery(id+"F5.wireOp",EDGE,"E33.MirrorCS")}),-1.0]])]});
            extrude(context, id + "F6", {"entities" : qUnion([Q0, Q1]), "operationType" : NewBodyOperationType.ADD, "oppositeDirection" : true, "depth" : 22 * mm, "hasSecondDirection" : true, "secondDirectionOppositeDirection" : true, "secondDirectionDepth" : 20 * mm});
        }
        {
            var Q0;
            Q0=qCreatedBy(makeId("Top.planeOp"),FACE);
            var sketch = newSketch(context, id + "F7", { "sketchPlane" : qUnion([Q0])});
            skCircle(sketch, "E41", {"center": v(-48.5, 12.5) * mm, "radius": 3.5 * mm});
            skCircle(sketch, "E42", {"center": v(6.5, 19) * mm, "radius": 1.5 * mm});
            skLineSegment(sketch, "E43", {"start": v(-29.25, 36.38) * mm, "end": v(-29.25, -16.2) * mm, "construction": true});
            skLineSegment(sketch, "E44", {"start": v(22.65, 12) * mm, "end": v(-84.49, 12) * mm, "construction": true});
            skCircle(sketch, "E45.MirrorC", {"center": v(-65, 19) * mm, "radius": 1.5 * mm});
            skCircle(sketch, "E46.MirrorC", {"center": v(-65, 5) * mm, "radius": 1.5 * mm});
            skCircle(sketch, "E47.MirrorC", {"center": v(6.5, 5) * mm, "radius": 1.5 * mm});
            skSolve(sketch);
        }
        {
            var Q0;
            Q0=makeQuery(id+"F7.imprint","IMPRINT",FACE,{"disambiguationData":[TD([[makeQuery(id+"F7.imprint","IMPRINT",EDGE,{"derivedFrom":sQuery(id+"F7.wireOp",EDGE,"E41")}),1.0]])]});
            extrude(context, id + "F8", {"entities" : qUnion([Q0]), "operationType" : NewBodyOperationType.REMOVE, "depth" : 5 * mm});
        }
        {
            var Q0;
            Q0=makeQuery(id+"F7.imprint","IMPRINT",FACE,{"disambiguationData":[TD([[makeQuery(id+"F7.imprint","IMPRINT",EDGE,{"derivedFrom":sQuery(id+"F7.wireOp",EDGE,"E45.MirrorC")}),-1.0]])]});
            var Q1;
            Q1=makeQuery(id+"F7.imprint","IMPRINT",FACE,{"disambiguationData":[TD([[makeQuery(id+"F7.imprint","IMPRINT",EDGE,{"derivedFrom":sQuery(id+"F7.wireOp",EDGE,"E46.MirrorC")}),1.0]])]});
            var Q2;
            Q2=makeQuery(id+"F7.imprint","IMPRINT",FACE,{"disambiguationData":[TD([[makeQuery(id+"F7.imprint","IMPRINT",EDGE,{"derivedFrom":sQuery(id+"F7.wireOp",EDGE,"E42")}),1.0]])]});
            var Q3;
            Q3=makeQuery(id+"F7.imprint","IMPRINT",FACE,{"disambiguationData":[TD([[makeQuery(id+"F7.imprint","IMPRINT",EDGE,{"derivedFrom":sQuery(id+"F7.wireOp",EDGE,"E47.MirrorC")}),-1.0]])]});
            extrude(context, id + "F9", {"entities" : qUnion([Q0, Q1, Q2, Q3]), "operationType" : NewBodyOperationType.REMOVE, "oppositeDirection" : true, "depth" : 32 * mm});
        }
        {
            var Q0;
            Q0=makeQuery(id+"F3.opExtrude","CAP_EDGE",EDGE,{"disambiguationData":[OSD([sQuery(id+"F0.wireOp",EDGE,"E4")])],"isStart":true});
            var Q1;
            Q1=makeQuery(id+"F3.opExtrude","CAP_EDGE",EDGE,{"disambiguationData":[OSD([sQuery(id+"F0.wireOp",EDGE,"E4")])],"isStart":false});
            var Q2;
            Q2=makeQuery(id+"F3.opExtrude","CAP_EDGE",EDGE,{"disambiguationData":[OSD([sQuery(id+"F0.wireOp",EDGE,"E10.MirrorCS")])],"isStart":true});
            var Q3;
            Q3=makeQuery(id+"F3.opExtrude","CAP_EDGE",EDGE,{"disambiguationData":[OSD([sQuery(id+"F0.wireOp",EDGE,"E10.MirrorCS")])],"isStart":false});
            fillet(context, id + "F10", {"entities" : qUnion([Q0, Q1, Q2, Q3]), "radius" : 4 * mm, "tangentPropagation" : true, "allowEdgeOverflow" : false});
        }
        {
            var Q0;
            Q0=makeQuery(id+"F0.imprint","IMPRINT",FACE,{"disambiguationData":[TD([[makeQuery(id+"F0.imprint","IMPRINT",EDGE,{"derivedFrom":sQuery(id+"F0.wireOp",EDGE,"E1.bottom")}),1.0]])]});
            extrude(context, id + "F11", {"entities" : qUnion([Q0]), "operationType" : NewBodyOperationType.ADD, "oppositeDirection" : true, "depth" : 5 * mm});
        }
        {
            var Q0;
            Q0=makeQuery(id+"F0.imprint","IMPRINT",FACE,{"disambiguationData":[TD([[makeQuery(id+"F0.imprint","IMPRINT",EDGE,{"derivedFrom":sQuery(id+"F0.wireOp",EDGE,"E17.bottom")}),1.0]])]});
            var Q1;
            Q1=makeQuery(id+"F0.imprint","IMPRINT",FACE,{"disambiguationData":[TD([[makeQuery(id+"F0.imprint","IMPRINT",EDGE,{"derivedFrom":sQuery(id+"F0.wireOp",EDGE,"E17.bottom")}),-1.0]])]});
            extrude(context, id + "F12", {"entities" : qUnion([Q0, Q1]), "oppositeDirection" : true, "depth" : 4 * mm, "hasSecondDirection" : true, "secondDirectionOppositeDirection" : true, "secondDirectionDepth" : 2 * mm});
        }
        {
            var Q0;
            Q0=makeQuery(id+"F0.imprint","IMPRINT",FACE,{"disambiguationData":[TD([[makeQuery(id+"F0.imprint","IMPRINT",EDGE,{"derivedFrom":sQuery(id+"F0.wireOp",EDGE,"E22.sketch_text.stroke-143")}),-1.0]])]});
            var Q1;
            Q1=makeQuery(id+"F0.imprint","IMPRINT",FACE,{"disambiguationData":[TD([[makeQuery(id+"F0.imprint","IMPRINT",EDGE,{"derivedFrom":sQuery(id+"F0.wireOp",EDGE,"E22.sketch_text.stroke-134")}),-1.0]])]});
            var Q2;
            Q2=makeQuery(id+"F0.imprint","IMPRINT",FACE,{"disambiguationData":[TD([[makeQuery(id+"F0.imprint","IMPRINT",EDGE,{"derivedFrom":sQuery(id+"F0.wireOp",EDGE,"E22.sketch_text.stroke-114")}),-1.0]])]});
            var Q3;
            Q3=makeQuery(id+"F0.imprint","IMPRINT",FACE,{"disambiguationData":[TD([[makeQuery(id+"F0.imprint","IMPRINT",EDGE,{"derivedFrom":sQuery(id+"F0.wireOp",EDGE,"E22.sketch_text.stroke-128")}),-1.0]])]});
            var Q4;
            Q4=makeQuery(id+"F0.imprint","IMPRINT",FACE,{"disambiguationData":[TD([[makeQuery(id+"F0.imprint","IMPRINT",EDGE,{"derivedFrom":sQuery(id+"F0.wireOp",EDGE,"E22.sketch_text.stroke-77")}),-1.0]])]});
            var Q5;
            Q5=makeQuery(id+"F0.imprint","IMPRINT",FACE,{"disambiguationData":[TD([[makeQuery(id+"F0.imprint","IMPRINT",EDGE,{"derivedFrom":sQuery(id+"F0.wireOp",EDGE,"E22.sketch_text.stroke-90")}),-1.0]])]});
            var Q6;
            Q6=makeQuery(id+"F0.imprint","IMPRINT",FACE,{"disambiguationData":[TD([[makeQuery(id+"F0.imprint","IMPRINT",EDGE,{"derivedFrom":sQuery(id+"F0.wireOp",EDGE,"E22.sketch_text.stroke-70")}),-1.0]])]});
            var Q7;
            Q7=makeQuery(id+"F0.imprint","IMPRINT",FACE,{"disambiguationData":[TD([[makeQuery(id+"F0.imprint","IMPRINT",EDGE,{"derivedFrom":sQuery(id+"F0.wireOp",EDGE,"E22.sketch_text.stroke-63")}),-1.0]])]});
            var Q8;
            Q8=makeQuery(id+"F0.imprint","IMPRINT",FACE,{"disambiguationData":[TD([[makeQuery(id+"F0.imprint","IMPRINT",EDGE,{"derivedFrom":sQuery(id+"F0.wireOp",EDGE,"E22.sketch_text.stroke-36")}),-1.0]])]});
            var Q9;
            Q9=makeQuery(id+"F0.imprint","IMPRINT",FACE,{"disambiguationData":[TD([[makeQuery(id+"F0.imprint","IMPRINT",EDGE,{"derivedFrom":sQuery(id+"F0.wireOp",EDGE,"E22.sketch_text.stroke-30")}),-1.0]])]});
            var Q10;
            Q10=makeQuery(id+"F0.imprint","IMPRINT",FACE,{"disambiguationData":[TD([[makeQuery(id+"F0.imprint","IMPRINT",EDGE,{"derivedFrom":sQuery(id+"F0.wireOp",EDGE,"E22.sketch_text.stroke-18")}),-1.0]])]});
            var Q11;
            Q11=makeQuery(id+"F0.imprint","IMPRINT",FACE,{"disambiguationData":[TD([[makeQuery(id+"F0.imprint","IMPRINT",EDGE,{"derivedFrom":sQuery(id+"F0.wireOp",EDGE,"E22.sketch_text.stroke-22")}),-1.0]])]});
            var Q12;
            Q12=makeQuery(id+"F0.imprint","IMPRINT",FACE,{"disambiguationData":[TD([[makeQuery(id+"F0.imprint","IMPRINT",EDGE,{"derivedFrom":sQuery(id+"F0.wireOp",EDGE,"E22.sketch_text.stroke-0")}),-1.0]])]});
            var Q13;
            Q13=makeQuery(id+"F0.imprint","IMPRINT",FACE,{"disambiguationData":[TD([[makeQuery(id+"F0.imprint","IMPRINT",EDGE,{"derivedFrom":sQuery(id+"F0.wireOp",EDGE,"E21.sketch_text.stroke-0")}),-1.0]])]});
            var Q14;
            Q14=makeQuery(id+"F0.imprint","IMPRINT",FACE,{"disambiguationData":[TD([[makeQuery(id+"F0.imprint","IMPRINT",EDGE,{"derivedFrom":sQuery(id+"F0.wireOp",EDGE,"E21.sketch_text.stroke-5")}),-1.0]])]});
            var Q15;
            Q15=makeQuery(id+"F0.imprint","IMPRINT",FACE,{"disambiguationData":[TD([[makeQuery(id+"F0.imprint","IMPRINT",EDGE,{"derivedFrom":sQuery(id+"F0.wireOp",EDGE,"E21.sketch_text.stroke-31")}),-1.0]])]});
            var Q16;
            Q16=makeQuery(id+"F0.imprint","IMPRINT",FACE,{"disambiguationData":[TD([[makeQuery(id+"F0.imprint","IMPRINT",EDGE,{"derivedFrom":sQuery(id+"F0.wireOp",EDGE,"E21.sketch_text.stroke-38")}),-1.0]])]});
            var Q17;
            Q17=makeQuery(id+"F0.imprint","IMPRINT",FACE,{"disambiguationData":[TD([[makeQuery(id+"F0.imprint","IMPRINT",EDGE,{"derivedFrom":sQuery(id+"F0.wireOp",EDGE,"E21.sketch_text.stroke-64")}),-1.0]])]});
            var Q18;
            Q18=makeQuery(id+"F0.imprint","IMPRINT",FACE,{"disambiguationData":[TD([[makeQuery(id+"F0.imprint","IMPRINT",EDGE,{"derivedFrom":sQuery(id+"F0.wireOp",EDGE,"E21.sketch_text.stroke-45")}),-1.0]])]});
            var Q19;
            Q19=makeQuery(id+"F0.imprint","IMPRINT",FACE,{"disambiguationData":[TD([[makeQuery(id+"F0.imprint","IMPRINT",EDGE,{"derivedFrom":sQuery(id+"F0.wireOp",EDGE,"E21.sketch_text.stroke-100")}),-1.0]])]});
            var Q20;
            Q20=makeQuery(id+"F0.imprint","IMPRINT",FACE,{"disambiguationData":[TD([[makeQuery(id+"F0.imprint","IMPRINT",EDGE,{"derivedFrom":sQuery(id+"F0.wireOp",EDGE,"E21.sketch_text.stroke-131")}),-1.0]])]});
            var Q21;
            Q21=makeQuery(id+"F0.imprint","IMPRINT",FACE,{"disambiguationData":[TD([[makeQuery(id+"F0.imprint","IMPRINT",EDGE,{"derivedFrom":sQuery(id+"F0.wireOp",EDGE,"E21.sketch_text.stroke-112")}),-1.0]])]});
            var Q22;
            Q22=makeQuery(id+"F0.imprint","IMPRINT",FACE,{"disambiguationData":[TD([[makeQuery(id+"F0.imprint","IMPRINT",EDGE,{"derivedFrom":sQuery(id+"F0.wireOp",EDGE,"E21.sketch_text.stroke-187")}),-1.0]])]});
            var Q23;
            Q23=makeQuery(id+"F0.imprint","IMPRINT",FACE,{"disambiguationData":[TD([[makeQuery(id+"F0.imprint","IMPRINT",EDGE,{"derivedFrom":sQuery(id+"F0.wireOp",EDGE,"E21.sketch_text.stroke-196")}),-1.0]])]});
            var Q24;
            Q24=makeQuery(id+"F0.imprint","IMPRINT",FACE,{"disambiguationData":[TD([[makeQuery(id+"F0.imprint","IMPRINT",EDGE,{"derivedFrom":sQuery(id+"F0.wireOp",EDGE,"E21.sketch_text.stroke-167")}),-1.0]])]});
            var Q25;
            Q25=makeQuery(id+"F0.imprint","IMPRINT",FACE,{"disambiguationData":[TD([[makeQuery(id+"F0.imprint","IMPRINT",EDGE,{"derivedFrom":sQuery(id+"F0.wireOp",EDGE,"E21.sketch_text.stroke-181")}),-1.0]])]});
            extrude(context, id + "F13", {"entities" : qUnion([Q0, Q1, Q2, Q3, Q4, Q5, Q6, Q7, Q8, Q9, Q10, Q11, Q12, Q13, Q14, Q15, Q16, Q17, Q18, Q19, Q20, Q21, Q22, Q23, Q24, Q25]), "operationType" : NewBodyOperationType.ADD, "oppositeDirection" : true, "depth" : 4 * mm});
        }
        {
            var Q0;
            {var subQ5=sQuery(id+"F0.wireOp",EDGE,"E23");Q0=makeQuery(id+"F0.imprint","IMPRINT",FACE,{"disambiguationData":[TD([[makeQuery(id+"F0.imprint","IMPRINT",EDGE,{"derivedFrom":subQ5}),1.0]])]});}
            var Q1;
            {var subQ5=sQuery(id+"F0.wireOp",EDGE,"E24");Q1=makeQuery(id+"F0.imprint","IMPRINT",FACE,{"disambiguationData":[TD([[makeQuery(id+"F0.imprint","IMPRINT",EDGE,{"derivedFrom":subQ5}),1.0]])]});}
            extrude(context, id + "F14", {"entities" : qUnion([Q0, Q1]), "operationType" : NewBodyOperationType.ADD, "oppositeDirection" : true, "depth" : 22 * mm});
        }
    });
